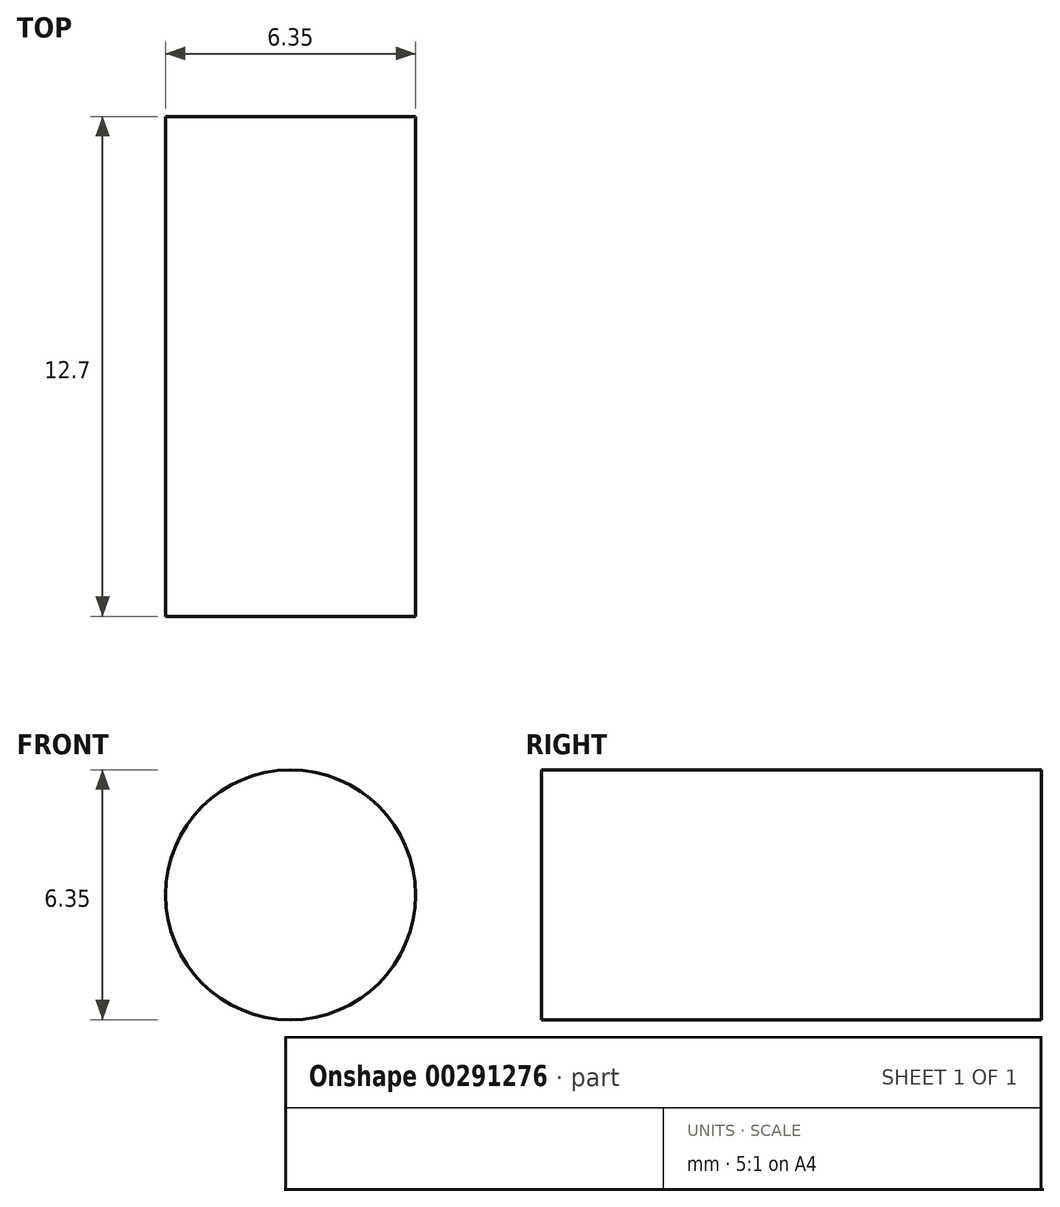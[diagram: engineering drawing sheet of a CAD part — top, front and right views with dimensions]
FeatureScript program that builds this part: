
annotation { "Feature Type Name" : "Feature", "Feature Type Description" : "" }
export const myFeature = defineFeature(function(context is Context, id is Id, definition is map)
    precondition{}
    {
        {
            var Q0;
            Q0=qCreatedBy(makeId("Front.planeOp"),FACE);
            var sketch = newSketch(context, id + "F0", { "sketchPlane" : qUnion([Q0])});
            skCircle(sketch, "E0", {"center": v(-33.09, 38.2) * mm, "radius": 3.18 * mm});
            skSolve(sketch);
        }
        {
            var Q0;
            Q0=makeQuery(id+"F0.imprint","IMPRINT",FACE,{"disambiguationData":[TD([[makeQuery(id+"F0.imprint","IMPRINT",EDGE,{"derivedFrom":sQuery(id+"F0.wireOp",EDGE,"E0")}),1.0]])]});
            extrude(context, id + "F1", {"entities" : qUnion([Q0]), "depth" : 12.7 * mm});
        }
    });
